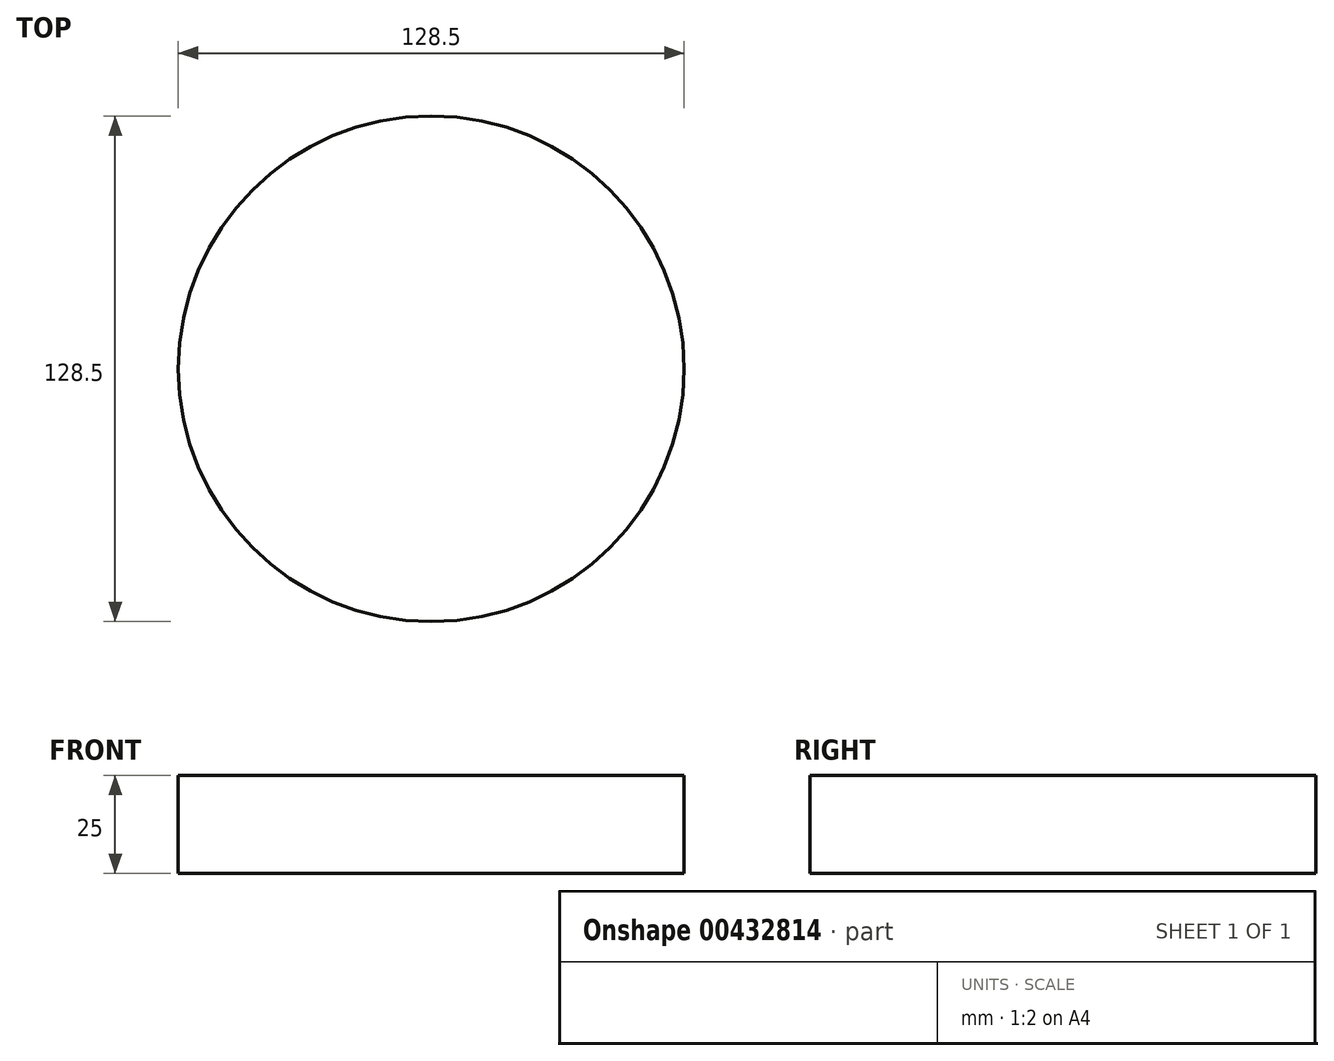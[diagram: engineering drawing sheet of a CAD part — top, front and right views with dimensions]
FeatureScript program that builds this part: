
annotation { "Feature Type Name" : "Feature", "Feature Type Description" : "" }
export const myFeature = defineFeature(function(context is Context, id is Id, definition is map)
    precondition{}
    {
        {
            var Q0;
            Q0=qCreatedBy(makeId("Top.planeOp"),FACE);
            var sketch = newSketch(context, id + "F0", { "sketchPlane" : qUnion([Q0])});
            skCircle(sketch, "E0", {"center": v(0, 0) * mm, "radius": 64.25 * mm});
            skSolve(sketch);
        }
        {
            var Q0;
            Q0=makeQuery(id+"F0.imprint","IMPRINT",FACE,{"disambiguationData":[TD([[makeQuery(id+"F0.imprint","IMPRINT",EDGE,{"derivedFrom":sQuery(id+"F0.wireOp",EDGE,"E0")}),1.0]])]});
            extrude(context, id + "F1", {"entities" : qUnion([Q0]), "depth" : 25 * mm});
        }
    });
